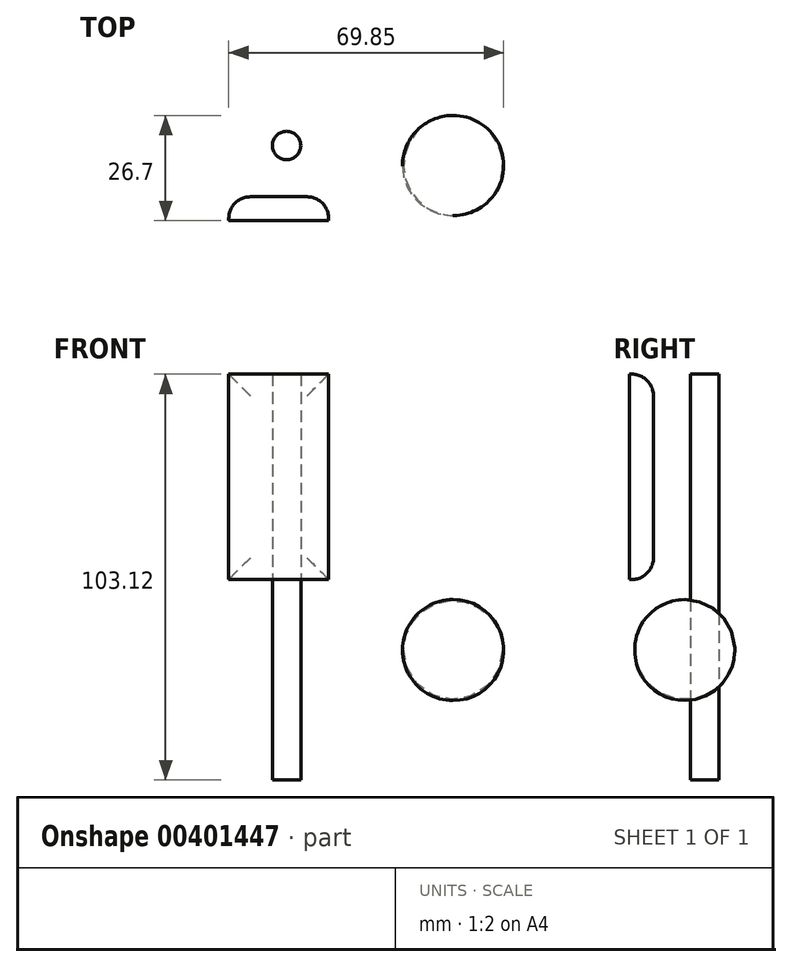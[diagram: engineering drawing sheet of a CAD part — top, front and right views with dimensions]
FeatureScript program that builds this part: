
annotation { "Feature Type Name" : "Feature", "Feature Type Description" : "" }
export const myFeature = defineFeature(function(context is Context, id is Id, definition is map)
    precondition{}
    {
        {
            var Q0;
            Q0=qCreatedBy(makeId("Top.planeOp"),FACE);
            var sketch = newSketch(context, id + "F0", { "sketchPlane" : qUnion([Q0])});
            skLineSegment(sketch, "E0.bottom", {"start": v(-23.82, -27.75) * mm, "end": v(1.58, -27.75) * mm});
            skLineSegment(sketch, "E0.top", {"start": v(-23.82, -21.7) * mm, "end": v(1.58, -21.7) * mm});
            skLineSegment(sketch, "E0.left", {"start": v(-23.82, -27.75) * mm, "end": v(-23.82, -21.7) * mm});
            skLineSegment(sketch, "E0.right", {"start": v(1.58, -27.75) * mm, "end": v(1.58, -21.7) * mm});
            skSolve(sketch);
        }
        {
            var Q0;
            Q0=qCreatedBy(makeId("Top.planeOp"),FACE);
            var sketch = newSketch(context, id + "F1", { "sketchPlane" : qUnion([Q0])});
            skLineSegment(sketch, "E1.bottom", {"start": v(-24.07, -19.45) * mm, "end": v(1.33, -19.45) * mm});
            skLineSegment(sketch, "E1.top", {"start": v(-24.07, -13.63) * mm, "end": v(1.33, -13.63) * mm});
            skLineSegment(sketch, "E1.left", {"start": v(-24.07, -19.45) * mm, "end": v(-24.07, -13.63) * mm});
            skLineSegment(sketch, "E1.right", {"start": v(1.33, -19.45) * mm, "end": v(1.33, -13.63) * mm});
            skSolve(sketch);
        }
        {
            var Q0;
            Q0=makeQuery(id+"F1.imprint","IMPRINT",FACE,{"disambiguationData":[TD([[makeQuery(id+"F1.imprint","IMPRINT",EDGE,{"derivedFrom":sQuery(id+"F1.wireOp",EDGE,"E1.bottom")}),1.0]])]});
            var Q1;
            Q1=makeQuery(id+"F0.imprint","IMPRINT",FACE,{"disambiguationData":[TD([[makeQuery(id+"F0.imprint","IMPRINT",EDGE,{"derivedFrom":sQuery(id+"F0.wireOp",EDGE,"E0.bottom")}),1.0]])]});
            extrude(context, id + "F2", {"entities" : qUnion([Q0, Q1]), "depth" : 25.4 * mm});
        }
        {
            var Q0;
            Q0=makeQuery(id+"F2.opExtrude","CAP_FACE",FACE,{"disambiguationData":[OSD([sQuery(id+"F0.wireOp",EDGE,"E0.bottom"),sQuery(id+"F0.wireOp",EDGE,"E0.top"),sQuery(id+"F0.wireOp",EDGE,"E0.left"),sQuery(id+"F0.wireOp",EDGE,"E0.right")])],"isStart":true});
            extrude(context, id + "F3", {"entities" : qUnion([Q0]), "operationType" : NewBodyOperationType.REMOVE, "oppositeDirection" : true, "depth" : 17.9 * mm});
        }
        {
            var Q0;
            Q0=makeQuery(id+"F2.opExtrude","CAP_FACE",FACE,{"disambiguationData":[OSD([sQuery(id+"F1.wireOp",EDGE,"E1.bottom"),sQuery(id+"F1.wireOp",EDGE,"E1.top"),sQuery(id+"F1.wireOp",EDGE,"E1.left"),sQuery(id+"F1.wireOp",EDGE,"E1.right")])],"isStart":true});
            extrude(context, id + "F4", {"entities" : qUnion([Q0]), "operationType" : NewBodyOperationType.REMOVE, "oppositeDirection" : true, "depth" : 23.24 * mm});
        }
        {
            var Q0;
            Q0=makeQuery(id+"F2.opExtrude","SWEPT_BODY",BODY,{"disambiguationData":[OSD([sQuery(id+"F1.wireOp",EDGE,"E1.bottom"),sQuery(id+"F1.wireOp",EDGE,"E1.top"),sQuery(id+"F1.wireOp",EDGE,"E1.left"),sQuery(id+"F1.wireOp",EDGE,"E1.right")])]});
            deleteBodies(context, id + "F5", {"entities" : qUnion([Q0])});
        }
        {
            var Q0;
            Q0=makeQuery(id+"F2.opExtrude","CAP_FACE",FACE,{"disambiguationData":[OSD([sQuery(id+"F0.wireOp",EDGE,"E0.bottom"),sQuery(id+"F0.wireOp",EDGE,"E0.top"),sQuery(id+"F0.wireOp",EDGE,"E0.left"),sQuery(id+"F0.wireOp",EDGE,"E0.right")])],"isStart":false});
            var sketch = newSketch(context, id + "F6", { "sketchPlane" : qUnion([Q0])});
            skCircle(sketch, "E2", {"center": v(-9.12, -8.67) * mm, "radius": 3.6 * mm});
            skSolve(sketch);
        }
        {
            var Q0;
            Q0 = qSketchRegion(id + "F6", true);
            var Q1;
            Q1=makeQuery(id+"F6.imprint","IMPRINT",FACE,{"disambiguationData":[TD([[makeQuery(id+"F6.imprint","IMPRINT",EDGE,{"derivedFrom":makeQuery(id+"F2.opExtrude","CAP_EDGE",EDGE,{"disambiguationData":[OSD([sQuery(id+"F0.wireOp",EDGE,"E0.bottom")])],"isStart":false})}),1.0]])]});
            extrude(context, id + "F7", {"entities" : qUnion([Q0, Q1]), "operationType" : NewBodyOperationType.ADD, "depth" : 44.7 * mm});
        }
        {
            var Q0;
            Q0=makeQuery(id+"F7.opExtrude","CAP_FACE",FACE,{"disambiguationData":[OSD([sQuery(id+"F0.wireOp",EDGE,"E0.bottom"),sQuery(id+"F0.wireOp",EDGE,"E0.top"),sQuery(id+"F0.wireOp",EDGE,"E0.left"),sQuery(id+"F0.wireOp",EDGE,"E0.right")])],"isStart":false});
            extrude(context, id + "F8", {"entities" : qUnion([Q0]), "operationType" : NewBodyOperationType.ADD, "oppositeDirection" : true, "depth" : 27.7 * mm});
        }
        {
            var Q0;
            Q0=qCreatedBy(makeId("Top.planeOp"),FACE);
            var sketch = newSketch(context, id + "F9", { "sketchPlane" : qUnion([Q0])});
            skArc(sketch, "E3", {"start": v(33.33, -26.45) * mm, "mid": v(46.03, -13.6) * mm, "end": v(33.04, -1.05) * mm});
            skLineSegment(sketch, "E4", {"start": v(33.04, -1.05) * mm, "end": v(33.33, -26.45) * mm});
            skSolve(sketch);
        }
        {
            var Q0;
            Q0=makeQuery(id+"F9.imprint","IMPRINT",FACE,{"disambiguationData":[TD([[makeQuery(id+"F9.imprint","IMPRINT",EDGE,{"derivedFrom":sQuery(id+"F9.wireOp",EDGE,"E3")}),1.0]])]});
            var Q1;
            Q1=sQuery(id+"F9.wireOp",EDGE,"E4");
            revolve(context, id + "F10", {"entities" : qUnion([Q0]), "axis" : qUnion([Q1]), "revolveType" : RevolveType.FULL});
        }
        {
            var Q0;
            Q0=makeQuery(id+"F7.opExtrude","CAP_FACE",FACE,{"disambiguationData":[OSD([sQuery(id+"F6.wireOp",EDGE,"E2")])],"isStart":true});
            extrude(context, id + "F11", {"entities" : qUnion([Q0]), "operationType" : NewBodyOperationType.ADD, "depth" : 58.42 * mm});
        }
        {
            var Q0;
            {var subQ0=sQuery(id+"F0.wireOp",EDGE,"E0.top");Q0=makeQuery(id+"F7.boolean.opBoolean","MERGE",FACE,{"derivedFrom":[makeQuery(id+"F2.opExtrude","SWEPT_FACE",FACE,{"disambiguationData":[OSD([subQ0])]}),makeQuery(id+"F7.opExtrude","SWEPT_FACE",FACE,{"disambiguationData":[OSD([subQ0])]})]});}
            fillet(context, id + "F12", {"entities" : qUnion([Q0]), "radius" : 5.52 * mm, "tangentPropagation" : true, "allowEdgeOverflow" : false});
        }
    });
